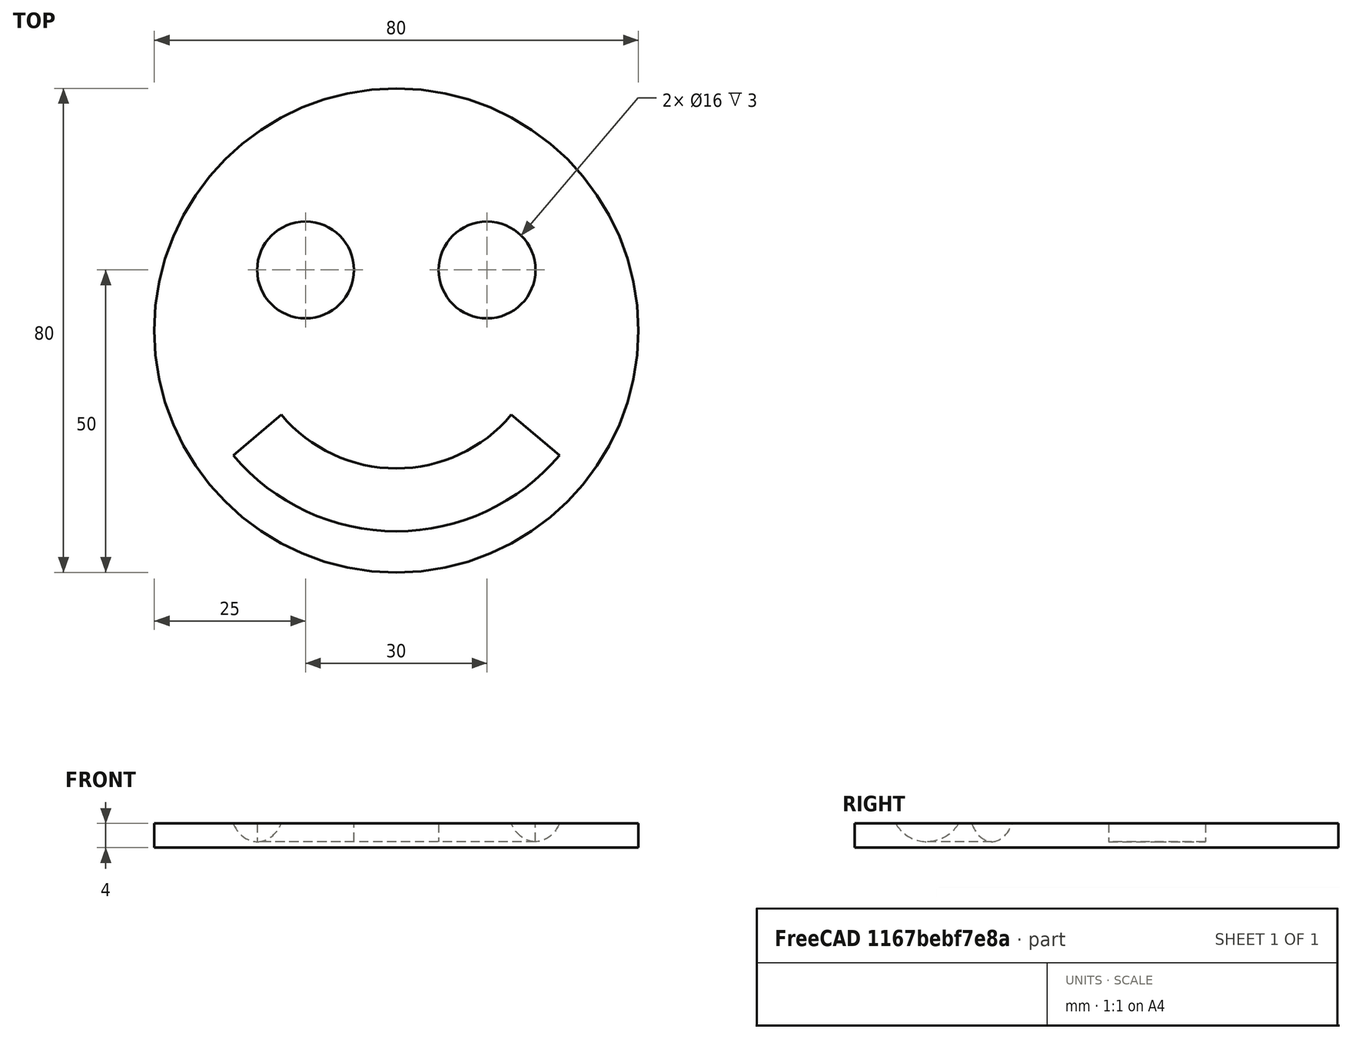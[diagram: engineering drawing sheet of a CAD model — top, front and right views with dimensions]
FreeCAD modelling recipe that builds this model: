
FCSTD DOCUMENT  (FreeCAD 0.21R33694 (Git))
Label: OJT1_T15R01_carita_feliz
License: All rights reserved
LicenseURL: http://en.wikipedia.org/wiki/All_rights_reserved
objects: Part::Cylinder×3, Part::Cut×3, Part::Torus×1
note: 7 computed .brp shape members not serialized (recipe doc carries the construction recipe); baked Part::Feature solids carry a one-line shape summary decoded from their .brp

FEATURE [Part::Cylinder] Cylinder
  Angle = 360
  AttacherType = Attacher::AttachEngine3D
  FirstAngle = 0
  Height = 4
  Radius = 40
  SecondAngle = 0
FEATURE [Part::Cylinder] Cylinder001
  Angle = 360
  AttacherType = Attacher::AttachEngine3D
  FirstAngle = 0
  Height = 10
  Placement = pos=(-15,10,1) rot=(0,0,1;0rad)
  Radius = 8
  SecondAngle = 0
FEATURE [Part::Cylinder] Cylinder002
  Angle = 360
  AttacherType = Attacher::AttachEngine3D
  FirstAngle = 0
  Height = 10
  Placement = pos=(15,10,1) rot=(0,0,1;0rad)
  Radius = 8
  SecondAngle = 0
FEATURE [Part::Cut] Cut
  Base = -> Cylinder
  Refine = true
  Tool = -> Cylinder001
FEATURE [Part::Cut] Cut001
  Base = -> Cut
  Refine = true
  Tool = -> Cylinder002
FEATURE [Part::Torus] Torus
  Angle1 = -180
  Angle2 = 180
  Angle3 = 100
  AttacherType = Attacher::AttachEngine3D
  Placement = pos=(0,2,7) rot=(0,0,-1;2.44346rad)
  Radius1 = 30
  Radius2 = 6
FEATURE [Part::Cut] Cut002
  Base = -> Cut001
  Refine = true
  Tool = -> Torus
